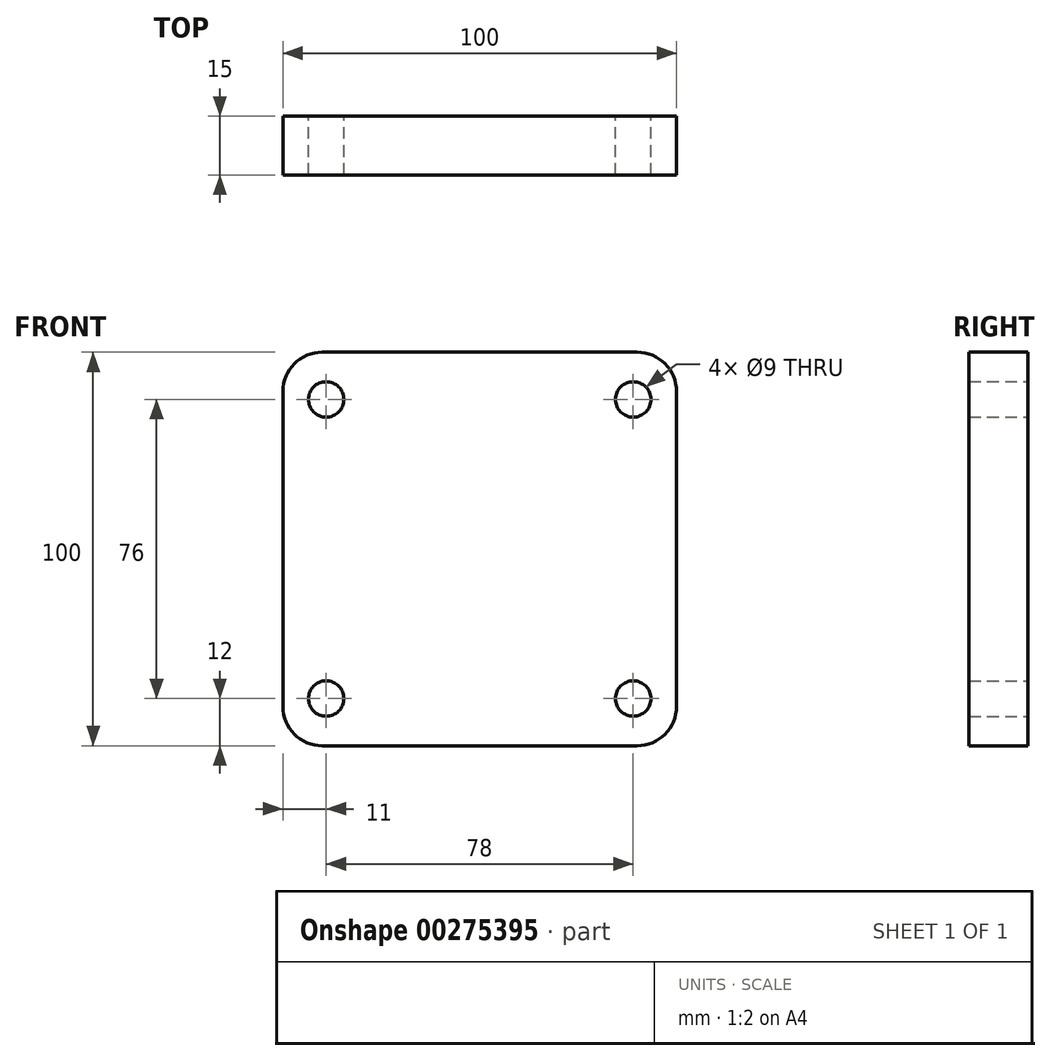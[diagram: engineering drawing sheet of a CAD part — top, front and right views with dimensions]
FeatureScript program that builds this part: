
annotation { "Feature Type Name" : "Feature", "Feature Type Description" : "" }
export const myFeature = defineFeature(function(context is Context, id is Id, definition is map)
    precondition{}
    {
        {
            var Q0;
            Q0=qCreatedBy(makeId("Front.planeOp"),FACE);
            var sketch = newSketch(context, id + "F0", { "sketchPlane" : qUnion([Q0])});
            skLineSegment(sketch, "E0.bottom", {"start": v(-40, 50) * mm, "end": v(40, 50) * mm});
            skLineSegment(sketch, "E0.top", {"start": v(-40, -50) * mm, "end": v(40, -50) * mm});
            skLineSegment(sketch, "E0.left", {"start": v(-50, 40) * mm, "end": v(-50, -40) * mm});
            skLineSegment(sketch, "E0.right", {"start": v(50, 40) * mm, "end": v(50, -40) * mm});
            skPoint(sketch, "E1.visualSharp", {"position": v(-50, 50) * mm});
            skArc(sketch, "E1.filletArc", {"start": v(-40, 50) * mm, "mid": v(-47.07, 47.07) * mm, "end": v(-50, 40) * mm});
            skPoint(sketch, "E2.visualSharp", {"position": v(50, 50) * mm});
            skArc(sketch, "E2.filletArc", {"start": v(50, 40) * mm, "mid": v(47.07, 47.07) * mm, "end": v(40, 50) * mm});
            skPoint(sketch, "E3.visualSharp", {"position": v(50, -50) * mm});
            skArc(sketch, "E3.filletArc", {"start": v(40, -50) * mm, "mid": v(47.07, -47.07) * mm, "end": v(50, -40) * mm});
            skPoint(sketch, "E4.visualSharp", {"position": v(-50, -50) * mm});
            skArc(sketch, "E4.filletArc", {"start": v(-50, -40) * mm, "mid": v(-47.07, -47.07) * mm, "end": v(-40, -50) * mm});
            skCircle(sketch, "E5", {"center": v(-39, 38) * mm, "radius": 4.5 * mm});
            skCircle(sketch, "E6", {"center": v(39, 38) * mm, "radius": 4.5 * mm});
            skCircle(sketch, "E7", {"center": v(-39, -38) * mm, "radius": 4.5 * mm});
            skCircle(sketch, "E8", {"center": v(39, -38) * mm, "radius": 4.5 * mm});
            skSolve(sketch);
        }
        {
            var Q0;
            Q0=makeQuery(id+"F0.imprint","IMPRINT",FACE,{"disambiguationData":[TD([[makeQuery(id+"F0.imprint","IMPRINT",EDGE,{"derivedFrom":sQuery(id+"F0.wireOp",EDGE,"E0.bottom")}),-1.0]])]});
            extrude(context, id + "F1", {"entities" : qUnion([Q0]), "depth" : 15 * mm});
        }
    });
